# Revit family: Furniture-Mirror-KOHLER-Essential-K-26052
name_source: partatom
category: Specialty Equipment
revit_build: Autodesk Revit 2017 (Build: 20160225_1515(x64)
units: mm (PartAtom-declared; Revit-internal decimal feet)

## family parameters
Cut with Voids When Loaded = No
Host = Face
OmniClass Number = 23.21.37.13.15
OmniClass Title = Mirrors
Part Type = Normal
Room Calculation Point = No
Round Connector Dimension = Use Diameter
Shared = No

## types (4) — shared parameters
ADA Compliant = No
Assembly Code = E20
Date Modified = 12/08/2020
Default Elevation = 60"
Description = Rectangle Mirror 22inch * 34inch
Height = 34 1/16"
Length = 1 3/8"
Manufacturer = KOHLER Co.
Master Format 2014 = 08 83 00
Master Format 2014 Name = Mirrors
Material = Aluminium
Product Documentation Link = https://www.us.kohler.com
Product Name = Essential
Product Page URL = http://www.us.kohler.com
URL = https://www.us.kohler.com
WaterSense Certified = No
Width = 22"

## per-type parameters (varying)
| type | Finish | Model | Type |
| BLL-Matte Black | KOHLER-Metal-BLL-Matte_Black | K-26052-BLL | 1 |
| BGL-Moderne Brushed Gold | KOHLER-Metal-BGL-Moderne_Brushed_Gold | K-26052-BGL | 2 |
| BNL-Brushed Nickel | KOHLER-Metal-BNL-Brushed_Nickel | K-26052-BNL | 3 |
| CPL-Polished Chrome | KOHLER-Metal-CPL-Polished_Chrome | K-26052-CPL | 4 |

## geometry (parser evidence)
native form markers: Sweep x4
no freeform markers — native parametric forms only
